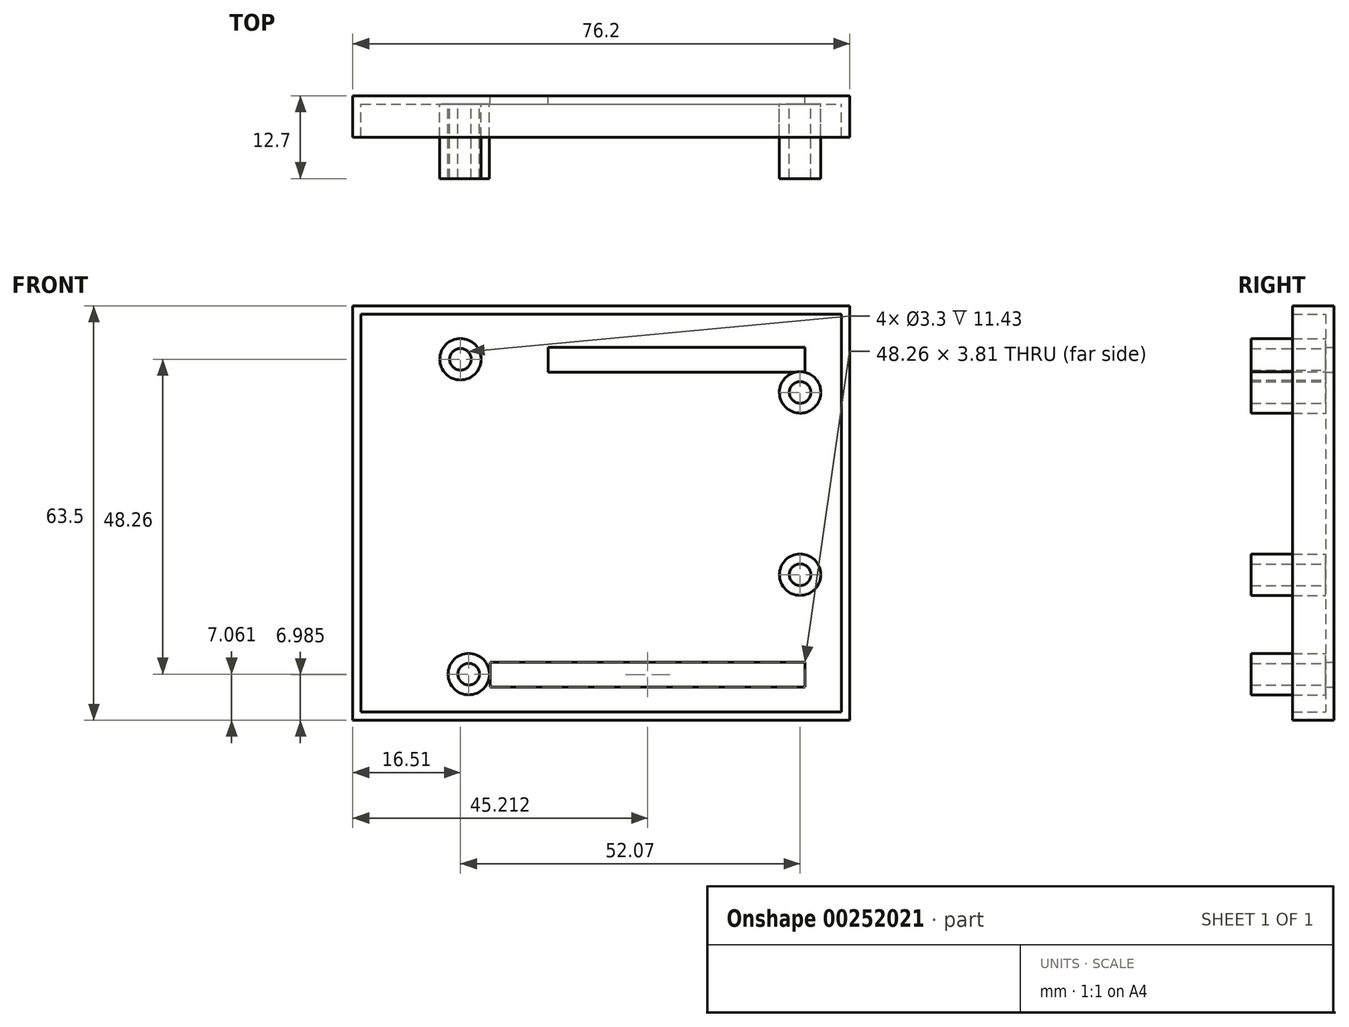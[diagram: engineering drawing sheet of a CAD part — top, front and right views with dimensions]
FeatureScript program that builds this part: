
annotation { "Feature Type Name" : "Feature", "Feature Type Description" : "" }
export const myFeature = defineFeature(function(context is Context, id is Id, definition is map)
    precondition{}
    {
        {
            var Q0;
            Q0=qCreatedBy(makeId("Front.planeOp"),FACE);
            var sketch = newSketch(context, id + "F0", { "sketchPlane" : qUnion([Q0])});
            skLineSegment(sketch, "E0.bottom", {"start": v(0, 63.5) * mm, "end": v(76.2, 63.5) * mm});
            skLineSegment(sketch, "E0.top", {"start": v(0, 0) * mm, "end": v(76.2, 0) * mm});
            skLineSegment(sketch, "E0.left", {"start": v(0, 63.5) * mm, "end": v(0, 0) * mm});
            skLineSegment(sketch, "E0.right", {"start": v(76.2, 63.5) * mm, "end": v(76.2, 0) * mm});
            skSolve(sketch);
        }
        {
            var Q0;
            Q0=makeQuery(id+"F0.imprint","IMPRINT",FACE,{"disambiguationData":[TD([[makeQuery(id+"F0.imprint","IMPRINT",EDGE,{"derivedFrom":sQuery(id+"F0.wireOp",EDGE,"brBC3KbL-EG9J-vsdL-SePl-hzVDqoBTHbGP")}),1.0]])]});
            var Q1;
            Q1=makeQuery(id+"F0.imprint","IMPRINT",FACE,{"disambiguationData":[TD([[makeQuery(id+"F0.imprint","IMPRINT",EDGE,{"derivedFrom":sQuery(id+"F0.wireOp",EDGE,"BntW7quv-2HLz-dvJl-wQES-wXUxCfIMOkLv")}),1.0]])]});
            var Q2;
            Q2=makeQuery(id+"F0.imprint","IMPRINT",FACE,{"disambiguationData":[TD([[makeQuery(id+"F0.imprint","IMPRINT",EDGE,{"derivedFrom":sQuery(id+"F0.wireOp",EDGE,"aSzLEpmf-ETZK-BwI2-V2vw-FS7RvumS7vd2")}),1.0]])]});
            var Q3;
            Q3=makeQuery(id+"F0.imprint","IMPRINT",FACE,{"disambiguationData":[TD([[makeQuery(id+"F0.imprint","IMPRINT",EDGE,{"derivedFrom":sQuery(id+"F0.wireOp",EDGE,"Ap6Lo27P-b6BO-CC3j-8LaT-OWlvdygEvpYj")}),1.0]])]});
            var Q4;
            Q4=makeQuery(id+"F0.imprint","IMPRINT",FACE,{"disambiguationData":[TD([[makeQuery(id+"F0.imprint","IMPRINT",EDGE,{"derivedFrom":sQuery(id+"F0.wireOp",EDGE,"E0.bottom")}),-1.0]])]});
            extrude(context, id + "F1", {"entities" : qUnion([Q0, Q1, Q2, Q3, Q4]), "depth" : 6.35 * mm});
        }
        {
            var Q0;
            Q0=makeQuery(id+"F1.opExtrude","CAP_FACE",FACE,{"disambiguationData":[OSD([sQuery(id+"F0.wireOp",EDGE,"E0.bottom"),sQuery(id+"F0.wireOp",EDGE,"E0.top"),sQuery(id+"F0.wireOp",EDGE,"E0.left"),sQuery(id+"F0.wireOp",EDGE,"E0.right")])],"isStart":false});
            var Q1;
            Q1=makeQuery(id+"F1.opExtrude","SWEPT_BODY",BODY,{"disambiguationData":[OSD([sQuery(id+"F0.wireOp",EDGE,"E0.bottom"),sQuery(id+"F0.wireOp",EDGE,"E0.top"),sQuery(id+"F0.wireOp",EDGE,"E0.left"),sQuery(id+"F0.wireOp",EDGE,"E0.right")])]});
            shell(context, id + "F2", {"entities" : qUnion([Q0]), "parts" : qUnion([Q1]), "thickness" : 1.27 * mm});
        }
        {
            var Q0;
            Q0=makeQuery(id+"F2.opShell","OFFSET_FACE",FACE,{"disambiguationData":[OSD([sQuery(id+"F0.wireOp",EDGE,"E0.bottom"),sQuery(id+"F0.wireOp",EDGE,"E0.top"),sQuery(id+"F0.wireOp",EDGE,"E0.left"),sQuery(id+"F0.wireOp",EDGE,"E0.right")])]});
            var sketch = newSketch(context, id + "F3", { "sketchPlane" : qUnion([Q0])});
            skCircle(sketch, "E1", {"center": v(16.51, 55.32) * mm, "radius": 1.65 * mm});
            skCircle(sketch, "E2", {"center": v(68.58, 50.24) * mm, "radius": 1.65 * mm});
            skCircle(sketch, "E3", {"center": v(68.58, 22.3) * mm, "radius": 1.65 * mm});
            skCircle(sketch, "E4", {"center": v(17.78, 7.06) * mm, "radius": 1.65 * mm});
            skCircle(sketch, "E5", {"center": v(16.51, 55.32) * mm, "radius": 3.18 * mm});
            skCircle(sketch, "E6", {"center": v(68.58, 50.24) * mm, "radius": 3.18 * mm});
            skCircle(sketch, "E7", {"center": v(68.58, 22.3) * mm, "radius": 3.18 * mm});
            skCircle(sketch, "E8", {"center": v(17.78, 7.06) * mm, "radius": 3.18 * mm});
            skSolve(sketch);
        }
        {
            var Q0;
            Q0 = qSketchRegion(id + "F3", true);
            var Q1;
            Q1=sQuery(id+"F3.wireOp",EDGE,"E1");
            var Q2;
            Q2=sQuery(id+"F3.wireOp",EDGE,"E2");
            var Q3;
            Q3=sQuery(id+"F3.wireOp",EDGE,"E4");
            var Q4;
            Q4=sQuery(id+"F3.wireOp",EDGE,"E3");
            extrude(context, id + "F4", {"entities" : qUnion([Q0]), "operationType" : NewBodyOperationType.ADD, "surfaceEntities" : qUnion([Q1, Q2, Q3, Q4]), "depth" : 11.43 * mm});
        }
        {
            var Q0;
            Q0=makeQuery(id+"F1.opExtrude","CAP_FACE",FACE,{"disambiguationData":[OSD([sQuery(id+"F0.wireOp",EDGE,"E0.bottom"),sQuery(id+"F0.wireOp",EDGE,"E0.top"),sQuery(id+"F0.wireOp",EDGE,"E0.left"),sQuery(id+"F0.wireOp",EDGE,"E0.right")])],"isStart":true});
            var sketch = newSketch(context, id + "F5", { "sketchPlane" : qUnion([Q0])});
            skLineSegment(sketch, "E9.bottom", {"start": v(-21.08, 5.08) * mm, "end": v(-69.34, 5.08) * mm});
            skLineSegment(sketch, "E9.top", {"start": v(-21.08, 8.9) * mm, "end": v(-69.34, 8.89) * mm});
            skLineSegment(sketch, "E9.left", {"start": v(-21.08, 5.08) * mm, "end": v(-21.08, 8.9) * mm});
            skLineSegment(sketch, "E9.right", {"start": v(-69.34, 5.08) * mm, "end": v(-69.34, 8.89) * mm});
            skLineSegment(sketch, "E10.bottom", {"start": v(-29.97, 53.34) * mm, "end": v(-69.34, 53.34) * mm});
            skLineSegment(sketch, "E10.top", {"start": v(-29.97, 57.15) * mm, "end": v(-69.34, 57.15) * mm});
            skLineSegment(sketch, "E10.left", {"start": v(-29.97, 53.34) * mm, "end": v(-29.97, 57.15) * mm});
            skLineSegment(sketch, "E10.right", {"start": v(-69.34, 53.34) * mm, "end": v(-69.34, 57.15) * mm});
            skSolve(sketch);
        }
        {
            var Q0;
            Q0 = qSketchRegion(id + "F5", true);
            extrude(context, id + "F6", {"entities" : qUnion([Q0]), "operationType" : NewBodyOperationType.REMOVE, "oppositeDirection" : true, "depth" : 1.27 * mm});
        }
    });
